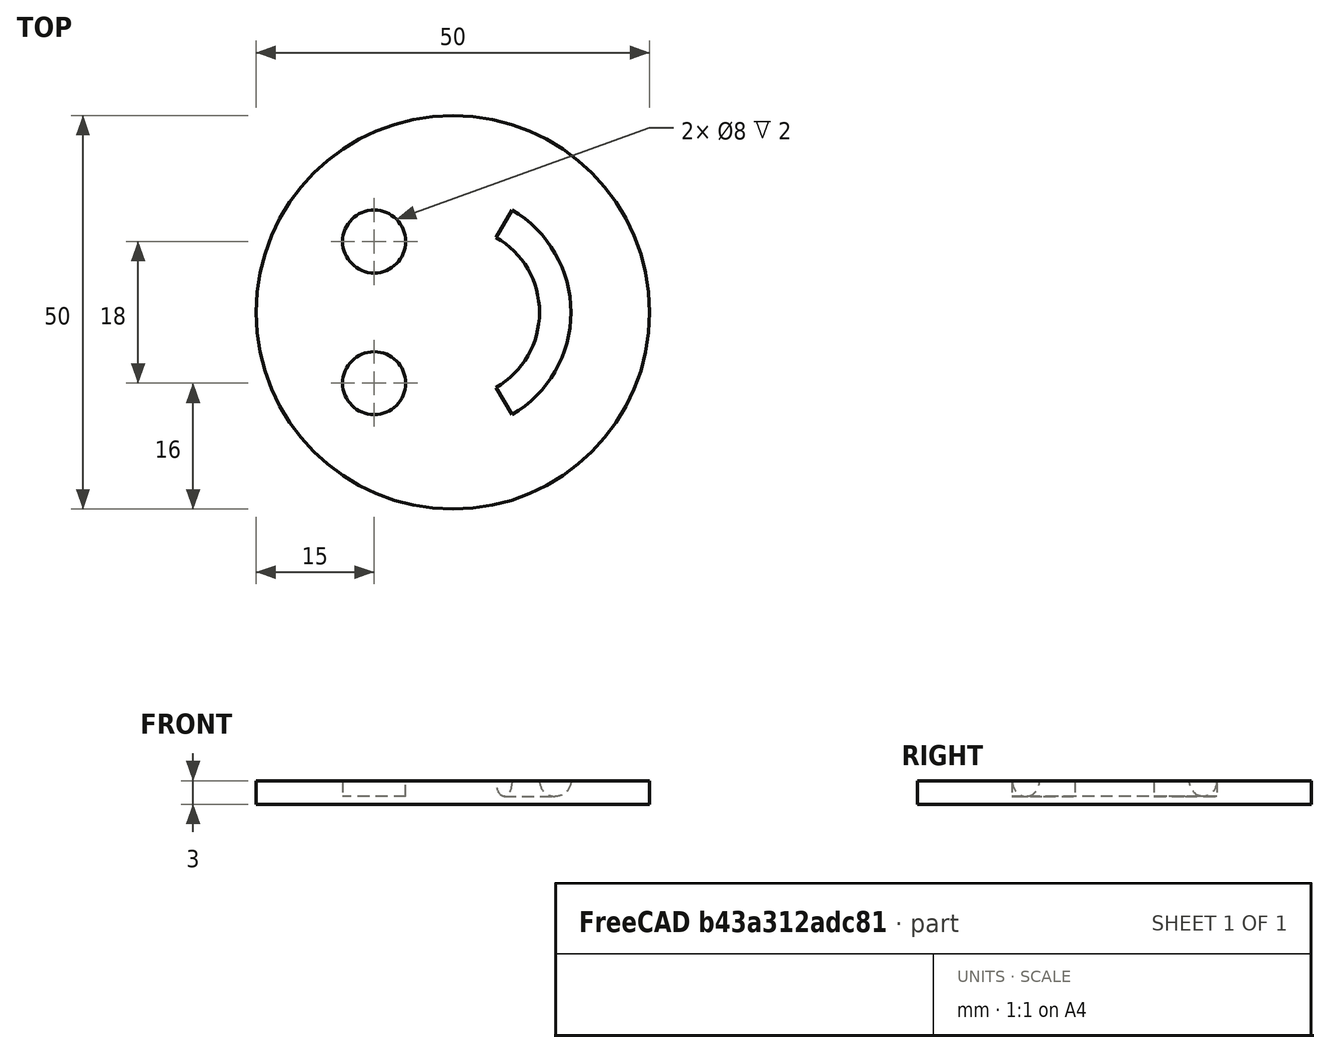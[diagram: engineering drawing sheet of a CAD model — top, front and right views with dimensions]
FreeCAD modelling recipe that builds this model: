
FCSTD DOCUMENT  (FreeCAD 0.21R33694 (Git))
Label: OJT1_T15P02.happy_face
License: All rights reserved
LicenseURL: http://en.wikipedia.org/wiki/All_rights_reserved
objects: Part::Cylinder×3, Part::Cut×2, Part::Torus×1, Part::Fuse×1
note: 7 computed .brp shape members not serialized (recipe doc carries the construction recipe); baked Part::Feature solids carry a one-line shape summary decoded from their .brp

FEATURE [Part::Cylinder] Cylinder  label="Cilindre"
  Angle = 360
  AttacherType = Attacher::AttachEngine3D
  FirstAngle = 0
  Height = 3
  Radius = 25
  SecondAngle = 0
FEATURE [Part::Torus] Torus
  Angle1 = -180
  Angle2 = 180
  Angle3 = 120
  AttacherType = Attacher::AttachEngine3D
  Placement = pos=(0,0,3) rot=(0,0,-1;1.0472rad)
  Radius1 = 13
  Radius2 = 2
FEATURE [Part::Cut] Cut
  Base = -> Cylinder
  Refine = true
  Tool = -> Torus
FEATURE [Part::Cylinder] Cylinder001  label="Cilindre001"
  Angle = 360
  AttacherType = Attacher::AttachEngine3D
  FirstAngle = 0
  Height = 3
  Placement = pos=(-10,9,1) rot=(0,0,1;0rad)
  Radius = 4
  SecondAngle = 0
FEATURE [Part::Cylinder] Cylinder002  label="Cilindre002"
  Angle = 360
  AttacherType = Attacher::AttachEngine3D
  FirstAngle = 0
  Height = 3
  Placement = pos=(-10,-9,1) rot=(0,0,1;0rad)
  Radius = 4
  SecondAngle = 0
FEATURE [Part::Fuse] Fusion
  Base = -> Cylinder001
  Refine = true
  Tool = -> Cylinder002
FEATURE [Part::Cut] Cut001
  Base = -> Cut
  Refine = true
  Tool = -> Fusion
